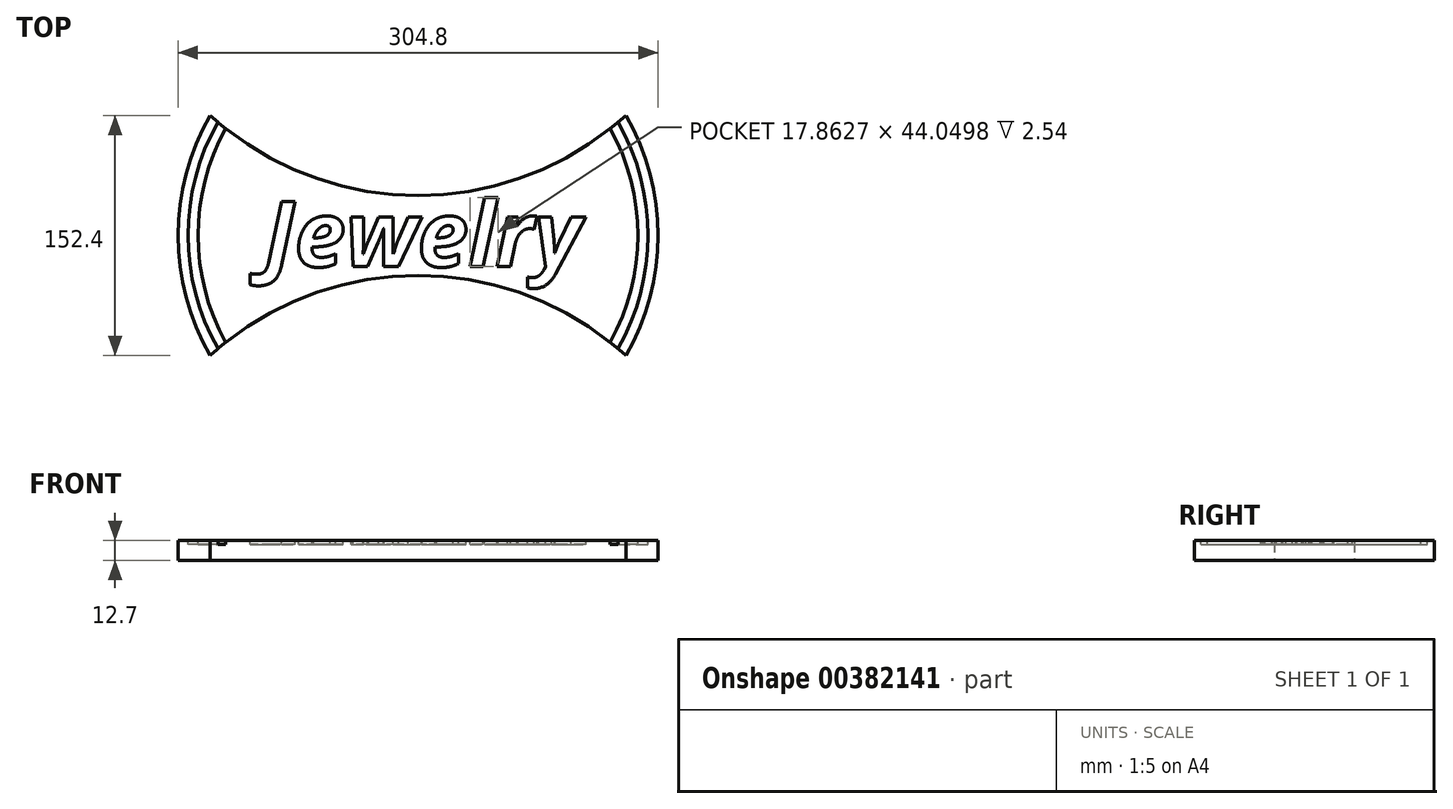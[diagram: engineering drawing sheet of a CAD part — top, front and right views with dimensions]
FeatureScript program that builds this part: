
annotation { "Feature Type Name" : "Feature", "Feature Type Description" : "" }
export const myFeature = defineFeature(function(context is Context, id is Id, definition is map)
    precondition{}
    {
        {
            var Q0;
            Q0=qCreatedBy(makeId("Top.planeOp"),FACE);
            var sketch = newSketch(context, id + "F0", { "sketchPlane" : qUnion([Q0])});
            skCircle(sketch, "E0", {"center": v(0, 0) * mm, "radius": 152.4 * mm});
            skLineSegment(sketch, "E1", {"start": v(0, 0) * mm, "end": v(0, 25.4) * mm});
            skLineSegment(sketch, "E2", {"start": v(0, 25.4) * mm, "end": v(0, 222.25) * mm});
            skCircle(sketch, "E3", {"center": v(0, 222.25) * mm, "radius": 196.85 * mm});
            skCircle(sketch, "E4.MirrorC", {"center": v(0, -222.25) * mm, "radius": 196.85 * mm});
            skSolve(sketch);
        }
        {
            var Q0;
            {var subQ0=sQuery(id+"F0.wireOp",EDGE,"E3");var subQ1=sQuery(id+"F0.wireOp",EDGE,"E0");var subQ2=makeQuery(id+"F0.imprint","INTERSECT",VERTEX,{"disambiguationData":[OD(0.0)],"derivedFrom":[subQ1,subQ0]});Q0=makeQuery(id+"F0.imprint","IMPRINT",FACE,{"disambiguationData":[TD([[makeQuery(id+"F0.imprint","IMPRINT",EDGE,{"disambiguationData":[TD([[subQ2,1.0]])],"derivedFrom":subQ1}),1.0]])]});}
            extrude(context, id + "F1", {"entities" : qUnion([Q0]), "depth" : 12.7 * mm});
        }
        {
            var Q0;
            Q0=makeQuery(id+"F1.opExtrude","CAP_FACE",FACE,{"disambiguationData":[OSD([sQuery(id+"F0.wireOp",EDGE,"E0"),sQuery(id+"F0.wireOp",EDGE,"E3"),sQuery(id+"F0.wireOp",EDGE,"E4.MirrorC")])],"isStart":false});
            var sketch = newSketch(context, id + "F2", { "sketchPlane" : qUnion([Q0])});
            skText(sketch, "E5", { "text": "Jewelry", "fontName": "OpenSans-BoldItalic.ttf"});
            const initialGuessF2  = {"E5": [-0.09758, -0.01983, 1, 0, 0.04174]};
            skSetInitialGuess(sketch, initialGuessF2);
            skSolve(sketch);
        }
        {
            var Q0;
            Q0 = qSketchRegion(id + "F2", true);
            extrude(context, id + "F3", {"entities" : qUnion([Q0]), "operationType" : NewBodyOperationType.REMOVE, "oppositeDirection" : true, "depth" : 2.54 * mm});
        }
        {
            var Q0;
            {var subQ0=sQuery(id+"F0.wireOp",EDGE,"E4.MirrorC");var subQ1=sQuery(id+"F0.wireOp",EDGE,"E3");var subQ2=sQuery(id+"F0.wireOp",EDGE,"E0");Q0=makeQuery(id+"F3.boolean.opBoolean","SPLIT",FACE,{"disambiguationData":[TD([makeQuery(id+"F1.opExtrude","SWEPT_FACE",FACE,{"disambiguationData":[OSD([subQ1])]})])],"derivedFrom":makeQuery(id+"F1.opExtrude","CAP_FACE",FACE,{"disambiguationData":[OSD([subQ2,subQ1,subQ0])],"isStart":false})});}
            var sketch = newSketch(context, id + "F4", { "sketchPlane" : qUnion([Q0])});
            skArc(sketch, "E6.0", {"start": v(-127.1, 71.94) * mm, "mid": v(-146.05, 0) * mm, "end": v(-127.1, -71.94) * mm});
            skArc(sketch, "E7.0", {"start": v(127.1, -71.94) * mm, "mid": v(146.05, 0) * mm, "end": v(127.1, 71.94) * mm});
            skArc(sketch, "E8.0", {"start": v(-122.11, 67.85) * mm, "mid": v(-139.7, 0) * mm, "end": v(-122.11, -67.85) * mm});
            skArc(sketch, "E9.0", {"start": v(-117.01, 63.95) * mm, "mid": v(-133.35, 0) * mm, "end": v(-117.01, -63.95) * mm});
            skArc(sketch, "E10.0", {"start": v(122.11, -67.85) * mm, "mid": v(139.7, 0) * mm, "end": v(122.11, 67.85) * mm});
            skArc(sketch, "E11.0", {"start": v(117.01, -63.95) * mm, "mid": v(133.35, 0) * mm, "end": v(117.01, 63.95) * mm});
            skSolve(sketch);
        }
        {
            var Q0;
            {var subQ0=sQuery(id+"F4.wireOp",EDGE,"E6.0");Q0=makeQuery(id+"F4.imprint","IMPRINT",FACE,{"disambiguationData":[TD([[makeQuery(id+"F4.imprint","IMPRINT",EDGE,{"derivedFrom":subQ0}),1.0]])]});}
            var Q1;
            {var subQ0=sQuery(id+"F4.wireOp",EDGE,"E7.0");Q1=makeQuery(id+"F4.imprint","IMPRINT",FACE,{"disambiguationData":[TD([[makeQuery(id+"F4.imprint","IMPRINT",EDGE,{"derivedFrom":subQ0}),1.0]])]});}
            extrude(context, id + "F5", {"entities" : qUnion([Q0, Q1]), "operationType" : NewBodyOperationType.REMOVE, "oppositeDirection" : true, "depth" : 2.54 * mm});
        }
    });
